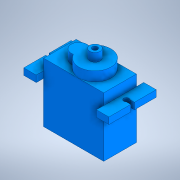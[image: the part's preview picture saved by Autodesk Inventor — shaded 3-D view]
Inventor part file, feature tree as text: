
AUTODESK INVENTOR PART (.ipt)
format: ipt  version: 2021.1 (Build 251245010, 245A)  size: 195,072 bytes
history: native  units: in
note: dims shown in document units (in); Inventor stores cm internally (conversion verified against a paired STEP export)
features: extrude x6, sketch x6, plane x5, mirror x2
ambient origin geometry x8: Origin, YZ Plane, XZ Plane, XY Plane, X Axis, Y Axis, Z Axis, Center Point
bodies: Solid1 (feature_tree)
feature tree (19):
  extrude  "Extrusion1"  Depth=0.4921in
  plane  "Work Plane3"
  plane  "Work Plane4"
  plane  "Work Plane5"
  extrude  "Extrusion2"  Depth=0.8937in
  mirror  "Mirror1"
  plane  "Work Plane6"
  extrude  "Extrusion3"  Depth=0.1102in
  extrude  "Extrusion4"  Depth=0.1102in
  extrude  "Extrusion5"  Depth=0.189in
  extrude  "Extrusion6"  Depth=0.0787in
  mirror  "Mirror2"
  sketch  "Sketch1"  dims[d0=0.9055in d1=0.4921in]
  plane  "Work Plane2"
  sketch  "Sketch2"  dims[d2=0.8937in d3=0.0in d4=0.4528in d5=-0.9055in d6=0.1969in d7=0.2461in]
  sketch  "Sketch3"  dims[d8=0.6299in d9=0.1102in]
  sketch  "Sketch4"  dims[d10=0.0984in d11=0.1102in]
  sketch  "Sketch5"  dims[d12=0.189in d13=0.0in d14=0.4331in]
  sketch  "Sketch6"  dims[d15=0.4173in d16=0.4803in d17=0.0787in d18=0.1575in d19=0.0in d20=0.1575in d21=0.126in d22=0.0in d23=0.126in d24=0.0in d25=0.0787in d26=0.0984in d27=0.0in d28=0.0787in]
